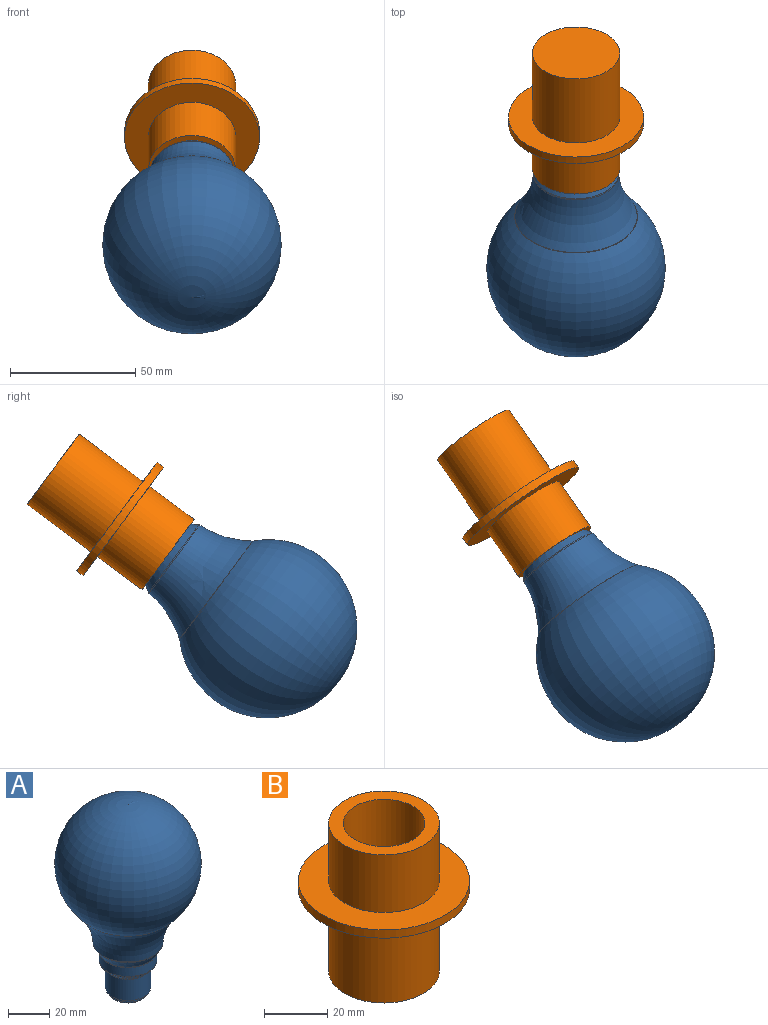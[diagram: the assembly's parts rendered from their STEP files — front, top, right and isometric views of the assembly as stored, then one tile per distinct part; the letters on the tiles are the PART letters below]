
ASSEMBLY  parts=2 mates=1
PART A: 16 faces, bbox 71.4x71.4x112 mm
  f0: torus R=54.7mm, axis (0,0,1), area 2760.8mm2, adj f9,f15
  f1: cone r=17mm half-angle=31deg, axis (0,0,1), area 516.6mm2, adj f9,f10
  f2: cylinder r=14mm len=28mm, axis (0,0,1), area 467mm2, adj f10,f11
  f3: cone r=14mm half-angle=45deg, axis (0,0,1), area 268.2mm2, adj f11,f12
  f4: cylinder r=11mm len=22mm, axis (0,0,1), area 869.9mm2, adj f5,f12
  f5: plane 22x22mm, normal (0,0,-1), area 33.8mm2, adj f4,f13
  f6: cylinder r=9.5mm len=19mm, axis (0,0,1), area 59.7mm2, adj f13,f14
  f7: plane 17x17mm, normal (0,0,-1), area 227mm2, adj f14
  f8: torus R=0.43mm, axis (0,0,1), area 13725.8mm2, adj f15
  f9: torus R=16.01mm, axis (0,0,-1), area 52.3mm2, adj f0,f1
  f10: torus R=15mm, axis (0,0,1), area 47.7mm2, adj f1,f2
  f11: torus R=13mm, axis (0,0,-1), area 68.6mm2, adj f2,f3
  f12: torus R=12mm, axis (0,0,1), area 54.8mm2, adj f3,f4
  f13: torus R=10.5mm, axis (0,0,1), area 97.3mm2, adj f5,f6
  f14: torus R=8.5mm, axis (0,0,1), area 90.2mm2, adj f6,f7
  f15: torus R=25.25mm, axis (0,0,1), area 27.1mm2, adj f0,f8
PART B: 9 faces, bbox 54x54x57.2 mm
  f0: cylinder r=17.46mm len=34.93mm, axis (0,0,-1), area 3483.6mm2, adj f1,f3
  f1: plane 34.93x34.93mm, normal (0,0,-1), area 958mm2, adj f0
  f2: plane 53.98x53.98mm, normal (0,0,1), area 1330.1mm2, adj f4,f5
  f3: plane 53.98x53.98mm, normal (0,0,-1), area 1330.1mm2, adj f0,f4
  f4: cylinder r=26.99mm len=53.98mm, axis (0,0,-1), area 538.4mm2, adj f2,f3
  f5: cylinder r=17.46mm len=34.93mm, axis (0,0,-1), area 2438.5mm2, adj f2,f6
  f6: plane 34.93x34.93mm, normal (0,0,1), area 435.6mm2, adj f5,f7
  f7: cylinder r=12.9mm len=25.79mm, axis (0,0,1), area 1800.8mm2, adj f6,f8
  f8: plane 25.79x25.79mm, normal (0,0,1), area 522.4mm2, adj f7
PLACE A rot(axis=(1,0,0),126.6deg) t=(143.77,-289.49,23.1)mm
PLACE B rot(axis=(1,0,0),126.6deg) t=(143.77,-220.33,74.43)mm
MATE slider A.f1 <-> B.f7  axis (0,-0.8,-0.6) through (143.77,-251.98,50.94)mm
